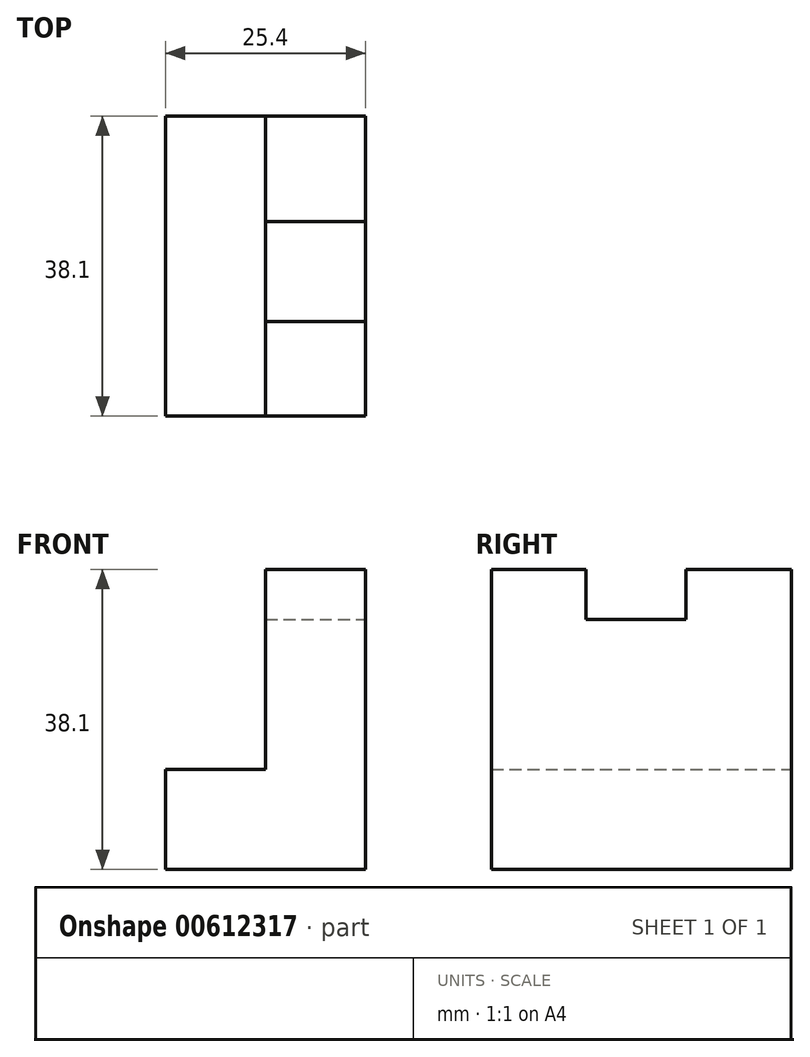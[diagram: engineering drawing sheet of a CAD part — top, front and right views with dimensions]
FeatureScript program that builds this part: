
annotation { "Feature Type Name" : "Feature", "Feature Type Description" : "" }
export const myFeature = defineFeature(function(context is Context, id is Id, definition is map)
    precondition{}
    {
        {
            var Q0;
            Q0=qCreatedBy(makeId("Front.planeOp"),FACE);
            var sketch = newSketch(context, id + "F0", { "sketchPlane" : qUnion([Q0])});
            skLineSegment(sketch, "E0", {"start": v(0, 0) * mm, "end": v(0, 12.7) * mm});
            skLineSegment(sketch, "E1", {"start": v(0, 12.7) * mm, "end": v(12.7, 12.7) * mm});
            skLineSegment(sketch, "E2", {"start": v(12.7, 12.7) * mm, "end": v(12.7, 31.75) * mm});
            skLineSegment(sketch, "E3", {"start": v(12.7, 31.75) * mm, "end": v(25.4, 31.75) * mm});
            skLineSegment(sketch, "E4", {"start": v(25.4, 31.75) * mm, "end": v(25.4, 0) * mm});
            skLineSegment(sketch, "E5", {"start": v(25.4, 0) * mm, "end": v(0, 0) * mm});
            skSolve(sketch);
        }
        {
            var Q0;
            Q0=qSketchRegion(id+"F0",true);
            extrude(context, id + "F1", {"entities" : qUnion([Q0]), "depth" : 38.1 * mm});
        }
        {
            var Q0;
            Q0=makeQuery(id+"F1.opExtrude","SWEPT_FACE",FACE,{"disambiguationData":[OSD([sQuery(id+"F0.wireOp",EDGE,"E3")])]});
            var sketch = newSketch(context, id + "F2", { "sketchPlane" : qUnion([Q0])});
            skLineSegment(sketch, "E6", {"start": v(12.7, 0) * mm, "end": v(12.7, -38.1) * mm});
            skLineSegment(sketch, "E7", {"start": v(12.7, -38.1) * mm, "end": v(25.4, -38.1) * mm});
            skLineSegment(sketch, "E8", {"start": v(25.4, -38.1) * mm, "end": v(25.4, 0) * mm});
            skLineSegment(sketch, "E9", {"start": v(25.4, 0) * mm, "end": v(12.7, 0) * mm});
            skLineSegment(sketch, "E10", {"start": v(12.7, -13.4) * mm, "end": v(25.4, -13.4) * mm});
            skLineSegment(sketch, "E11", {"start": v(25.4, -13.4) * mm, "end": v(25.4, -26.1) * mm});
            skLineSegment(sketch, "E12", {"start": v(25.4, -26.1) * mm, "end": v(12.7, -26.1) * mm});
            skLineSegment(sketch, "E13", {"start": v(12.7, -26.1) * mm, "end": v(12.7, -13.4) * mm});
            skSolve(sketch);
        }
        {
            var Q0;
            {var subQ0=sQuery(id+"F2.wireOp",EDGE,"E7");Q0=makeQuery(id+"F2.imprint","IMPRINT",FACE,{"disambiguationData":[TD([[makeQuery(id+"F2.imprint","IMPRINT",EDGE,{"derivedFrom":subQ0}),1.0]])]});}
            var Q1;
            {var subQ0=sQuery(id+"F2.wireOp",EDGE,"E9");Q1=makeQuery(id+"F2.imprint","IMPRINT",FACE,{"disambiguationData":[TD([[makeQuery(id+"F2.imprint","IMPRINT",EDGE,{"derivedFrom":subQ0}),-1.0]])]});}
            extrude(context, id + "F3", {"entities" : qUnion([Q0, Q1]), "operationType" : NewBodyOperationType.ADD, "depth" : 6.35 * mm});
        }
    });
